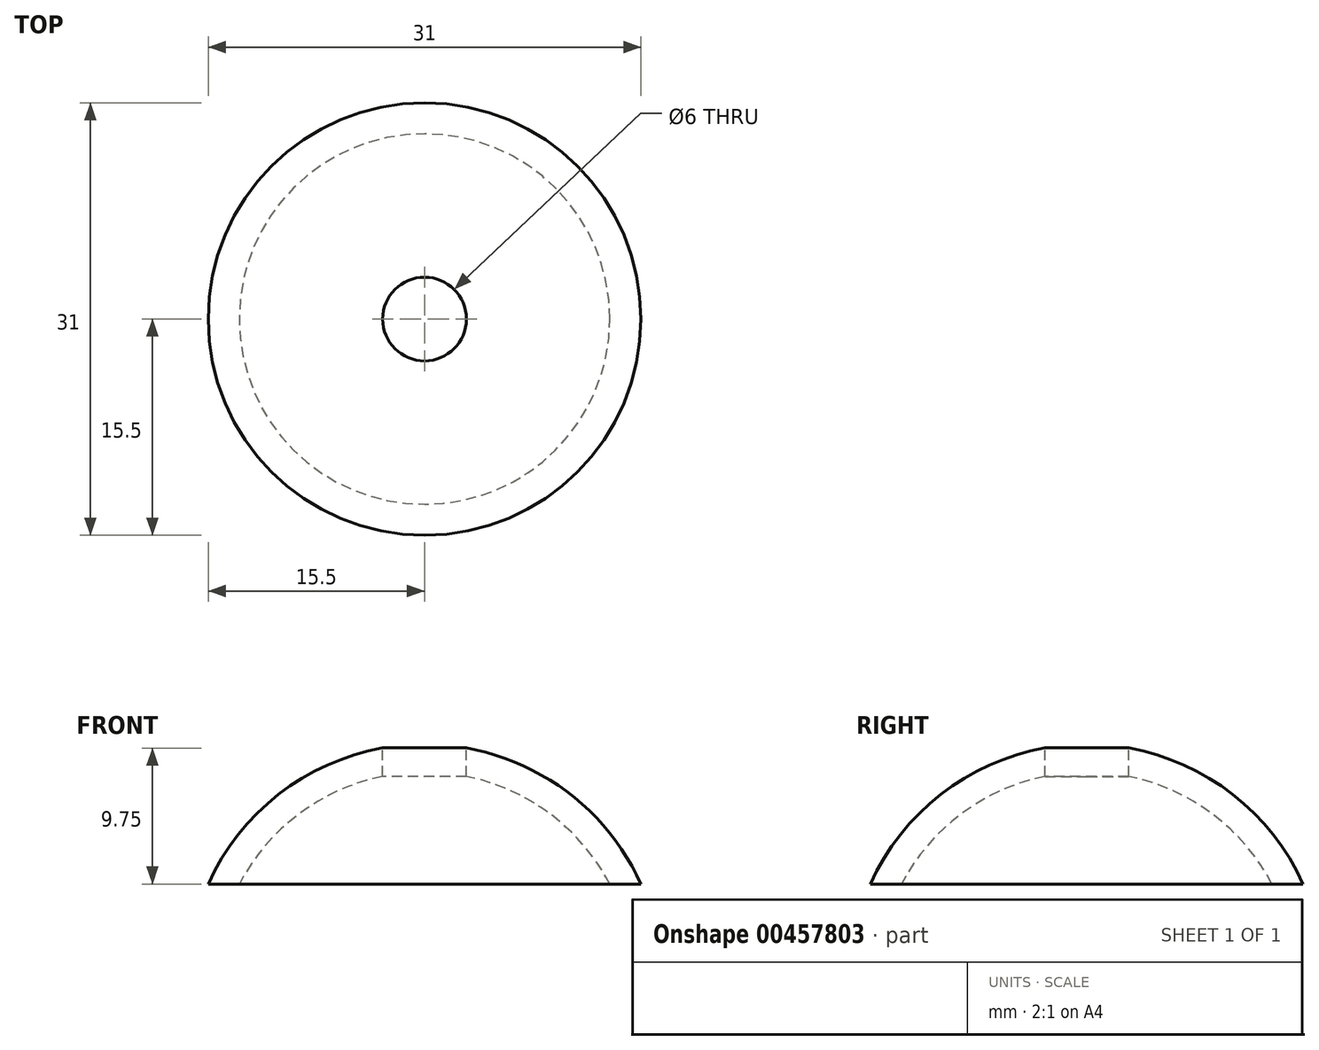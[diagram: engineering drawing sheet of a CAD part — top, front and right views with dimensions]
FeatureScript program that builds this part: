
annotation { "Feature Type Name" : "Feature", "Feature Type Description" : "" }
export const myFeature = defineFeature(function(context is Context, id is Id, definition is map)
    precondition{}
    {
        {
            var Q0;
            Q0=qCreatedBy(makeId("Front.planeOp"),FACE);
            var sketch = newSketch(context, id + "F0", { "sketchPlane" : qUnion([Q0])});
            skArc(sketch, "E0", {"start": v(13.28, 0) * mm, "mid": v(9, 5.01) * mm, "end": v(3, 7.71) * mm});
            skLineSegment(sketch, "E1", {"start": v(0, 0) * mm, "end": v(13.28, 0) * mm, "construction": true});
            skLineSegment(sketch, "E2", {"start": v(13.28, 0) * mm, "end": v(15.5, 0) * mm});
            skLineSegment(sketch, "E3.trimOffspring", {"start": v(0, 8.02) * mm, "end": v(0, -6.98) * mm, "construction": true});
            skArc(sketch, "E4.0", {"start": v(15.5, 0) * mm, "mid": v(10.46, 6.42) * mm, "end": v(3, 9.75) * mm});
            skLineSegment(sketch, "E5", {"start": v(3, 9.75) * mm, "end": v(3, 7.71) * mm});
            skSolve(sketch);
        }
        {
            var Q0;
            Q0=makeQuery(id+"F0.imprint","IMPRINT",FACE,{"disambiguationData":[TD([[makeQuery(id+"F0.imprint","IMPRINT",EDGE,{"derivedFrom":sQuery(id+"F0.wireOp",EDGE,"E0")}),-1.0]])]});
            var Q1;
            Q1=sQuery(id+"F0.wireOp",EDGE,"E3.trimOffspring");
            revolve(context, id + "F1", {"entities" : qUnion([Q0]), "axis" : qUnion([Q1]), "revolveType" : RevolveType.FULL});
        }
    });
